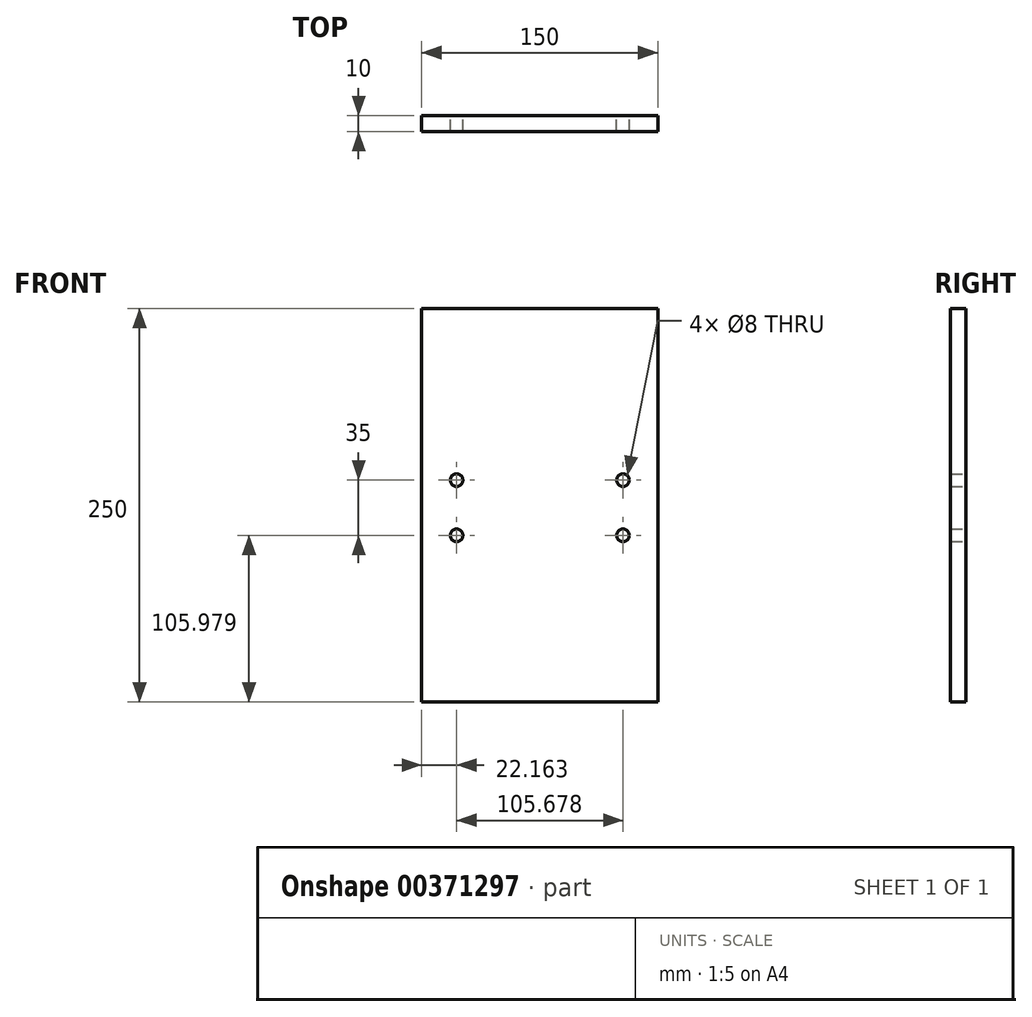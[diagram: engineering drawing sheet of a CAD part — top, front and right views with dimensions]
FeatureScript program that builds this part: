
annotation { "Feature Type Name" : "Feature", "Feature Type Description" : "" }
export const myFeature = defineFeature(function(context is Context, id is Id, definition is map)
    precondition{}
    {
        {
            var Q0;
            Q0=qCreatedBy(makeId("Front.planeOp"),FACE);
            var sketch = newSketch(context, id + "F0", { "sketchPlane" : qUnion([Q0])});
            skLineSegment(sketch, "E0.bottom", {"start": v(22.11, 44.86) * mm, "end": v(172.11, 44.86) * mm});
            skLineSegment(sketch, "E0.top", {"start": v(22.11, 294.86) * mm, "end": v(172.11, 294.86) * mm});
            skLineSegment(sketch, "E0.left", {"start": v(22.11, 44.86) * mm, "end": v(22.11, 294.86) * mm});
            skLineSegment(sketch, "E0.right", {"start": v(172.11, 44.86) * mm, "end": v(172.11, 294.86) * mm});
            skCircle(sketch, "E1", {"center": v(44.27, 185.84) * mm, "radius": 4 * mm});
            skLineSegment(sketch, "E2", {"start": v(97.11, 349.13) * mm, "end": v(97.11, 391.6) * mm, "construction": true});
            skPoint(sketch, "E2.startSnap0", {"position": v(97.11, 294.86) * mm});
            skCircle(sketch, "E3.MirrorC", {"center": v(149.95, 185.84) * mm, "radius": 4 * mm});
            skCircle(sketch, "E4", {"center": v(44.27, 150.84) * mm, "radius": 4 * mm});
            skCircle(sketch, "E5", {"center": v(149.95, 150.84) * mm, "radius": 4 * mm});
            skSolve(sketch);
        }
        {
            var Q0;
            Q0=makeQuery(id+"F0.imprint","IMPRINT",FACE,{"disambiguationData":[TD([[makeQuery(id+"F0.imprint","IMPRINT",EDGE,{"derivedFrom":sQuery(id+"F0.wireOp",EDGE,"E0.bottom")}),1.0]])]});
            extrude(context, id + "F1", {"entities" : qUnion([Q0]), "depth" : 10 * mm});
        }
    });
